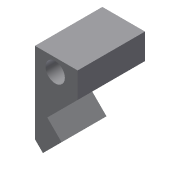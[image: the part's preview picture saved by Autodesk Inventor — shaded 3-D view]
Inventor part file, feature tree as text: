
AUTODESK INVENTOR PART (.ipt)
format: ipt  version: 2013 (Build 170138000, 138)  size: 131,584 bytes
history: native  units: mm
features: sketch x7, extrude x6, hole x1
ambient origin geometry x8: Origin, YZ Plane, XZ Plane, XY Plane, X Axis, Y Axis, Z Axis, Center Point
bodies: Solid1 (feature_tree)
feature tree (14):
  extrude  "Extrusion1"  Depth=20.0mm TaperAngle=0.0deg
  extrude  "Extrusion2"  Depth=3.8mm
  hole  "Hole1"  [1 undecoded]
  extrude  "Extrusion6"  Depth=0.5mm
  extrude  "Extrusion7"  Depth=0.5mm
  extrude  "Extrusion8"  Depth=15.0mm TaperAngle=0.0deg
  extrude  "Extrusion9"  Depth=1.0mm
  sketch  "Sketch1"  dims[d0=10.0mm d1=0.0mm d2=20.0mm d3=0.0mm]
  sketch  "Sketch2"  dims[d4=4.318mm d5=6.0mm d6=8.433mm d7=2.0mm d8=14.3117mm d9=31.0mm d10=20.594885mm d41=3.8mm]
  sketch  "Sketch3"  dims[d42=8.0mm d43=2.5mm d44=0.0mm]
  sketch  "Sketch8"  dims[d45=0.5mm d46=0.5mm]
  sketch  "Sketch9"  dims[d47=0.5mm d48=0.5mm]
  sketch  "Sketch10"  dims[d49=4.0mm d50=0.0mm d51=15.0mm d52=0.0mm]
  sketch  "Sketch11"  dims[d53=0.5mm d54=0.0mm d11=1.0mm d12=1.0mm d36=1.0mm d37=1.0mm]
note: 1 required parameter value undecoded (feature->parameter linkage not recoverable at this tier; creation-order binding heuristic only, values carry confidence <= 0.55)
